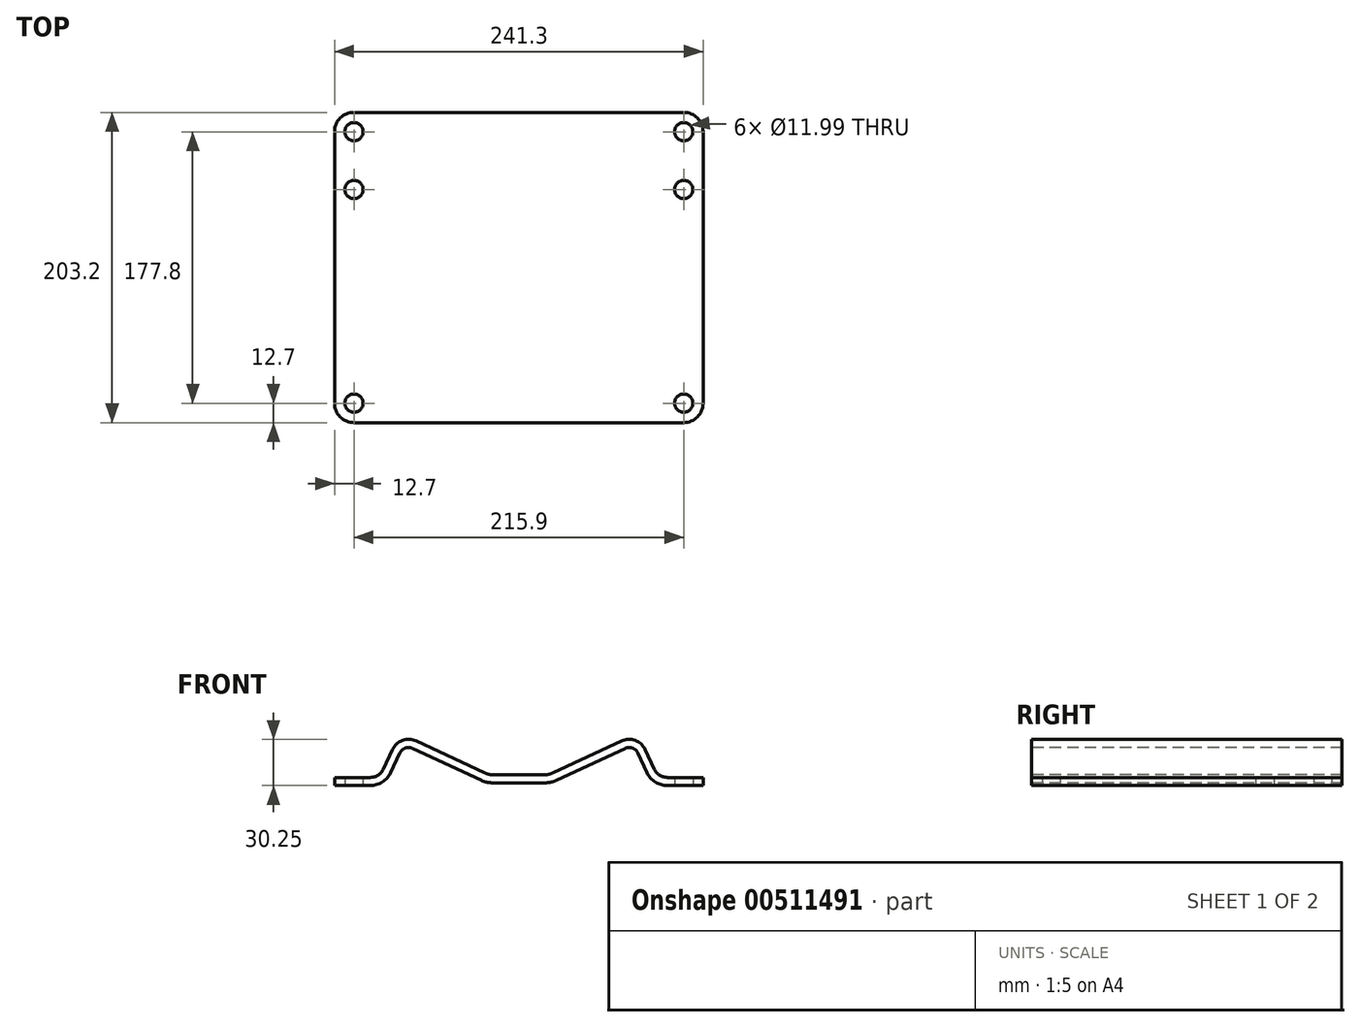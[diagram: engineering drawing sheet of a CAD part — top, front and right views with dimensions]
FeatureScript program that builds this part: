
annotation { "Feature Type Name" : "Feature", "Feature Type Description" : "" }
export const myFeature = defineFeature(function(context is Context, id is Id, definition is map)
    precondition{}
    {
        {
            var Q0;
            Q0=qCreatedBy(makeId("Front.planeOp"),FACE);
            var sketch = newSketch(context, id + "F0", { "sketchPlane" : qUnion([Q0])});
            skLineSegment(sketch, "E0", {"start": v(0, 0) * mm, "end": v(0, -131.98) * mm, "construction": true});
            skLineSegment(sketch, "E1", {"start": v(0, 0) * mm, "end": v(51.4, -110.22) * mm, "construction": true});
            skLineSegment(sketch, "E2", {"start": v(19.93, -124.9) * mm, "end": v(77.83, -97.9) * mm});
            skLineSegment(sketch, "E3", {"start": v(87.87, -131.98) * mm, "end": v(120.65, -131.98) * mm});
            skLineSegment(sketch, "E4.0", {"start": v(0, -124.9) * mm, "end": v(19.93, -124.9) * mm});
            skLineSegment(sketch, "E5", {"start": v(93.73, -131.98) * mm, "end": v(93.73, -104.3) * mm, "construction": true});
            skLineSegment(sketch, "E6.0", {"start": v(91.25, -126.67) * mm, "end": v(120.65, -126.67) * mm});
            skLineSegment(sketch, "E7", {"start": v(91.25, -126.67) * mm, "end": v(77.83, -97.9) * mm});
            skLineSegment(sketch, "E8", {"start": v(120.65, -126.67) * mm, "end": v(120.65, -131.98) * mm});
            skLineSegment(sketch, "E9.0", {"start": v(87.87, -131.98) * mm, "end": v(75.26, -104.95) * mm});
            skLineSegment(sketch, "E10.0", {"start": v(21.11, -130.2) * mm, "end": v(75.26, -104.95) * mm});
            skLineSegment(sketch, "E11.0", {"start": v(0, -130.2) * mm, "end": v(21.11, -130.2) * mm});
            skLineSegment(sketch, "E12.MirrorCS", {"start": v(-19.93, -124.9) * mm, "end": v(-77.83, -97.9) * mm});
            skLineSegment(sketch, "E13.MirrorCS", {"start": v(-91.25, -126.67) * mm, "end": v(-120.65, -126.67) * mm});
            skLineSegment(sketch, "E14.MirrorCS", {"start": v(-87.87, -131.98) * mm, "end": v(-75.26, -104.95) * mm});
            skLineSegment(sketch, "E15.MirrorCS", {"start": v(-87.87, -131.98) * mm, "end": v(-120.65, -131.98) * mm});
            skLineSegment(sketch, "E16.MirrorCS", {"start": v(-21.11, -130.2) * mm, "end": v(-75.26, -104.95) * mm});
            skLineSegment(sketch, "E17.MirrorCS", {"start": v(-93.73, -131.98) * mm, "end": v(-93.73, -104.3) * mm, "construction": true});
            skLineSegment(sketch, "E18.MirrorCS", {"start": v(0, -124.9) * mm, "end": v(-19.93, -124.9) * mm});
            skLineSegment(sketch, "E19.MirrorCS", {"start": v(-120.65, -126.67) * mm, "end": v(-120.65, -131.98) * mm});
            skLineSegment(sketch, "E20.MirrorCS", {"start": v(0, -130.2) * mm, "end": v(-21.11, -130.2) * mm});
            skLineSegment(sketch, "E21.MirrorCS", {"start": v(-91.25, -126.67) * mm, "end": v(-77.83, -97.9) * mm});
            skSolve(sketch);
        }
        {
            var Q0;
            Q0=makeQuery(id+"F0.imprint","IMPRINT",FACE,{"disambiguationData":[TD([[makeQuery(id+"F0.imprint","IMPRINT",EDGE,{"derivedFrom":sQuery(id+"F0.wireOp",EDGE,"E2")}),-1.0]])]});
            extrude(context, id + "F1", {"entities" : qUnion([Q0]), "oppositeDirection" : true, "depth" : 203.2 * mm, "offsetDistance" : 25.4 * mm});
        }
        {
            var Q0;
            Q0=makeQuery(id+"F1.opExtrude","SWEPT_FACE",FACE,{"disambiguationData":[OSD([sQuery(id+"F0.wireOp",EDGE,"E3")])]});
            var sketch = newSketch(context, id + "F2", { "sketchPlane" : qUnion([Q0])});
            skCircle(sketch, "E22", {"center": v(107.95, -12.7) * mm, "radius": 6 * mm});
            skLineSegment(sketch, "E23", {"start": v(107.95, -12.7) * mm, "end": v(107.95, -199.13) * mm, "construction": true});
            skCircle(sketch, "E24", {"center": v(107.95, -152.68) * mm, "radius": 6 * mm});
            skCircle(sketch, "E25", {"center": v(107.95, -190.5) * mm, "radius": 6 * mm});
            skCircle(sketch, "E26.1.0.0", {"center": v(-107.95, -12.7) * mm, "radius": 6 * mm});
            skCircle(sketch, "E26.1.0.1", {"center": v(-107.95, -152.68) * mm, "radius": 6 * mm});
            skCircle(sketch, "E26.1.0.2", {"center": v(-107.95, -190.5) * mm, "radius": 6 * mm});
            skLineSegment(sketch, "E26.direction1", {"start": v(107.95, -12.7) * mm, "end": v(-107.95, -12.7) * mm, "construction": true});
            skSolve(sketch);
        }
        {
            var Q0;
            Q0=makeQuery(id+"F2.imprint","IMPRINT",FACE,{"disambiguationData":[TD([[makeQuery(id+"F2.imprint","IMPRINT",EDGE,{"derivedFrom":sQuery(id+"F2.wireOp",EDGE,"E22")}),1.0]])]});
            var Q1;
            Q1=makeQuery(id+"F2.imprint","IMPRINT",FACE,{"disambiguationData":[TD([[makeQuery(id+"F2.imprint","IMPRINT",EDGE,{"derivedFrom":sQuery(id+"F2.wireOp",EDGE,"E24")}),1.0]])]});
            var Q2;
            Q2=makeQuery(id+"F2.imprint","IMPRINT",FACE,{"disambiguationData":[TD([[makeQuery(id+"F2.imprint","IMPRINT",EDGE,{"derivedFrom":sQuery(id+"F2.wireOp",EDGE,"E25")}),1.0]])]});
            var Q3;
            Q3=makeQuery(id+"F2.imprint","IMPRINT",FACE,{"disambiguationData":[TD([[makeQuery(id+"F2.imprint","IMPRINT",EDGE,{"derivedFrom":sQuery(id+"F2.wireOp",EDGE,"E26.1.0.2")}),1.0]])]});
            var Q4;
            Q4=makeQuery(id+"F2.imprint","IMPRINT",FACE,{"disambiguationData":[TD([[makeQuery(id+"F2.imprint","IMPRINT",EDGE,{"derivedFrom":sQuery(id+"F2.wireOp",EDGE,"E26.1.0.1")}),1.0]])]});
            var Q5;
            Q5=makeQuery(id+"F2.imprint","IMPRINT",FACE,{"disambiguationData":[TD([[makeQuery(id+"F2.imprint","IMPRINT",EDGE,{"derivedFrom":sQuery(id+"F2.wireOp",EDGE,"E26.1.0.0")}),1.0]])]});
            extrude(context, id + "F3", {"entities" : qUnion([Q0, Q1, Q2, Q3, Q4, Q5]), "operationType" : NewBodyOperationType.REMOVE, "endBound" : BoundingType.THROUGH_ALL, "oppositeDirection" : true, "depth" : 25.4 * mm, "offsetDistance" : 25.4 * mm});
        }
        {
            var Q0;
            Q0=makeQuery(id+"F1.opExtrude","SWEPT_EDGE",EDGE,{"disambiguationData":[OSD([sQuery(id+"F0.wireOp",EDGE,"E14.MirrorCS"),sQuery(id+"F0.wireOp",EDGE,"E16.MirrorCS")])]});
            var Q1;
            Q1=makeQuery(id+"F1.opExtrude","SWEPT_EDGE",EDGE,{"disambiguationData":[OSD([sQuery(id+"F0.wireOp",EDGE,"E9.0"),sQuery(id+"F0.wireOp",EDGE,"E10.0")])]});
            fillet(context, id + "F4", {"entities" : qUnion([Q0, Q1]), "radius" : 6.35 * mm, "tangentPropagation" : true, "allowEdgeOverflow" : false});
        }
        {
            var Q0;
            Q0=makeQuery(id+"F1.opExtrude","SWEPT_EDGE",EDGE,{"disambiguationData":[OSD([sQuery(id+"F0.wireOp",EDGE,"E2"),sQuery(id+"F0.wireOp",EDGE,"E7")])]});
            var Q1;
            Q1=makeQuery(id+"F1.opExtrude","SWEPT_EDGE",EDGE,{"disambiguationData":[OSD([sQuery(id+"F0.wireOp",EDGE,"E12.MirrorCS"),sQuery(id+"F0.wireOp",EDGE,"E21.MirrorCS")])]});
            fillet(context, id + "F5", {"entities" : qUnion([Q0, Q1]), "radius" : 11.66 * mm, "tangentPropagation" : true, "allowEdgeOverflow" : false});
        }
        {
            var Q0;
            Q0=makeQuery(id+"F1.opExtrude","SWEPT_EDGE",EDGE,{"disambiguationData":[OSD([sQuery(id+"F0.wireOp",EDGE,"E12.MirrorCS"),sQuery(id+"F0.wireOp",EDGE,"E18.MirrorCS")])]});
            var Q1;
            Q1=makeQuery(id+"F1.opExtrude","SWEPT_EDGE",EDGE,{"disambiguationData":[OSD([sQuery(id+"F0.wireOp",EDGE,"E2"),sQuery(id+"F0.wireOp",EDGE,"E4.0")])]});
            fillet(context, id + "F6", {"entities" : qUnion([Q0, Q1]), "radius" : 12.7 * mm, "tangentPropagation" : true, "allowEdgeOverflow" : false});
        }
        {
            var Q0;
            Q0=makeQuery(id+"F1.opExtrude","SWEPT_EDGE",EDGE,{"disambiguationData":[OSD([sQuery(id+"F0.wireOp",EDGE,"E16.MirrorCS"),sQuery(id+"F0.wireOp",EDGE,"E20.MirrorCS")])]});
            var Q1;
            Q1=makeQuery(id+"F1.opExtrude","SWEPT_EDGE",EDGE,{"disambiguationData":[OSD([sQuery(id+"F0.wireOp",EDGE,"E10.0"),sQuery(id+"F0.wireOp",EDGE,"E11.0")])]});
            fillet(context, id + "F7", {"entities" : qUnion([Q0, Q1]), "radius" : 18 * mm, "tangentPropagation" : true, "allowEdgeOverflow" : false});
        }
        {
            var Q0;
            Q0=makeQuery(id+"F1.opExtrude","SWEPT_EDGE",EDGE,{"disambiguationData":[OSD([sQuery(id+"F0.wireOp",EDGE,"E13.MirrorCS"),sQuery(id+"F0.wireOp",EDGE,"E21.MirrorCS")])]});
            var Q1;
            Q1=makeQuery(id+"F1.opExtrude","SWEPT_EDGE",EDGE,{"disambiguationData":[OSD([sQuery(id+"F0.wireOp",EDGE,"E6.0"),sQuery(id+"F0.wireOp",EDGE,"E7")])]});
            fillet(context, id + "F8", {"entities" : qUnion([Q0, Q1]), "radius" : 9.4 * mm, "tangentPropagation" : true, "allowEdgeOverflow" : false});
        }
        {
            var Q0;
            Q0=makeQuery(id+"F1.opExtrude","SWEPT_EDGE",EDGE,{"disambiguationData":[OSD([sQuery(id+"F0.wireOp",EDGE,"E14.MirrorCS"),sQuery(id+"F0.wireOp",EDGE,"E15.MirrorCS")])]});
            var Q1;
            Q1=makeQuery(id+"F1.opExtrude","SWEPT_EDGE",EDGE,{"disambiguationData":[OSD([sQuery(id+"F0.wireOp",EDGE,"E3"),sQuery(id+"F0.wireOp",EDGE,"E9.0")])]});
            fillet(context, id + "F9", {"entities" : qUnion([Q0, Q1]), "radius" : 14.7 * mm, "tangentPropagation" : true, "allowEdgeOverflow" : false});
        }
        {
            var Q0;
            Q0=makeQuery(id+"F1.opExtrude","CAP_EDGE",EDGE,{"disambiguationData":[OSD([sQuery(id+"F0.wireOp",EDGE,"E19.MirrorCS")])],"isStart":true});
            var Q1;
            Q1=makeQuery(id+"F1.opExtrude","CAP_EDGE",EDGE,{"disambiguationData":[OSD([sQuery(id+"F0.wireOp",EDGE,"E8")])],"isStart":true});
            var Q2;
            Q2=makeQuery(id+"F1.opExtrude","CAP_EDGE",EDGE,{"disambiguationData":[OSD([sQuery(id+"F0.wireOp",EDGE,"E19.MirrorCS")])],"isStart":false});
            var Q3;
            Q3=makeQuery(id+"F1.opExtrude","CAP_EDGE",EDGE,{"disambiguationData":[OSD([sQuery(id+"F0.wireOp",EDGE,"E8")])],"isStart":false});
            fillet(context, id + "F10", {"entities" : qUnion([Q0, Q1, Q2, Q3]), "radius" : 12.7 * mm, "tangentPropagation" : true, "allowEdgeOverflow" : false});
        }
    });
